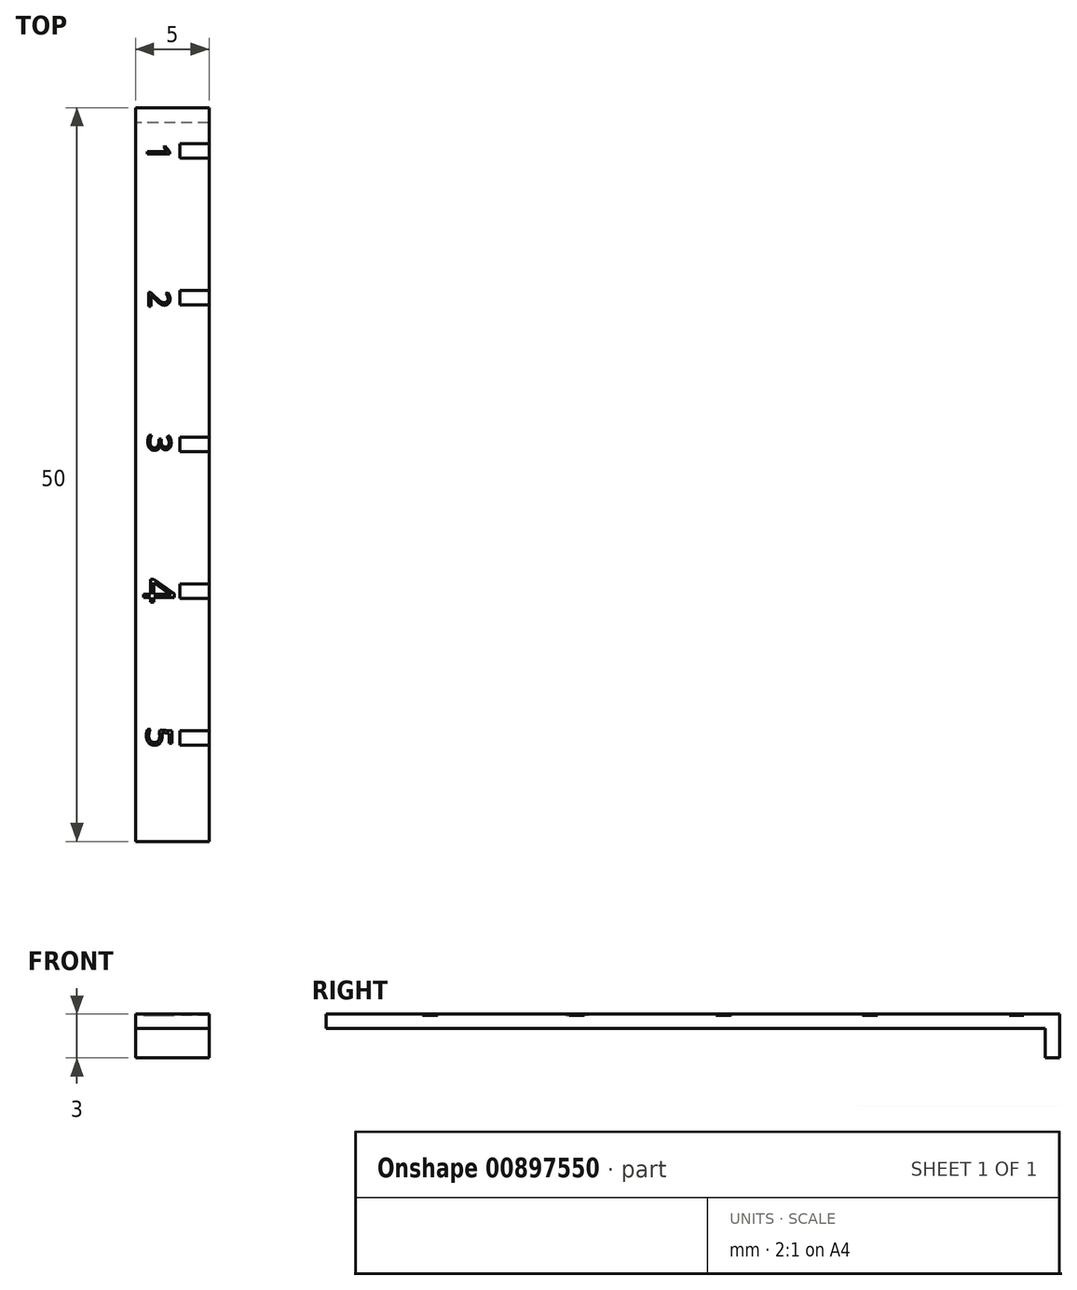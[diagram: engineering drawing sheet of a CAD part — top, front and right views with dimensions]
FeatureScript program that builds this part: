
annotation { "Feature Type Name" : "Feature", "Feature Type Description" : "" }
export const myFeature = defineFeature(function(context is Context, id is Id, definition is map)
    precondition{}
    {
        {
            var Q0;
            Q0=qCreatedBy(makeId("Top.planeOp"),FACE);
            var sketch = newSketch(context, id + "F0", { "sketchPlane" : qUnion([Q0])});
            skLineSegment(sketch, "E0.bottom", {"start": v(-33.65, 38.49) * mm, "end": v(-28.65, 38.49) * mm});
            skLineSegment(sketch, "E0.top", {"start": v(-33.65, -11.51) * mm, "end": v(-28.65, -11.51) * mm});
            skLineSegment(sketch, "E0.left", {"start": v(-33.65, 38.49) * mm, "end": v(-33.65, -11.51) * mm});
            skLineSegment(sketch, "E0.right", {"start": v(-28.65, 38.49) * mm, "end": v(-28.65, -11.51) * mm});
            skSolve(sketch);
        }
        {
            var Q0;
            Q0 = qSketchRegion(id + "F0", true);
            extrude(context, id + "F1", {"entities" : qUnion([Q0]), "depth" : 1 * mm, "offsetDistance" : 25 * mm});
        }
        {
            var Q0;
            Q0=makeQuery(id+"F1.opExtrude","CAP_FACE",FACE,{"disambiguationData":[OSD([sQuery(id+"F0.wireOp",EDGE,"E0.bottom"),sQuery(id+"F0.wireOp",EDGE,"E0.top"),sQuery(id+"F0.wireOp",EDGE,"E0.left"),sQuery(id+"F0.wireOp",EDGE,"E0.right")])],"isStart":true});
            var sketch = newSketch(context, id + "F2", { "sketchPlane" : qUnion([Q0])});
            skLineSegment(sketch, "E1.bottom", {"start": v(-28.65, -38.49) * mm, "end": v(-33.65, -38.49) * mm});
            skLineSegment(sketch, "E1.top", {"start": v(-28.65, -37.49) * mm, "end": v(-33.65, -37.49) * mm});
            skLineSegment(sketch, "E1.left", {"start": v(-28.65, -38.49) * mm, "end": v(-28.65, -37.49) * mm});
            skLineSegment(sketch, "E1.right", {"start": v(-33.65, -38.49) * mm, "end": v(-33.65, -37.49) * mm});
            skSolve(sketch);
        }
        {
            var Q0;
            Q0 = qSketchRegion(id + "F2", true);
            extrude(context, id + "F3", {"entities" : qUnion([Q0]), "operationType" : NewBodyOperationType.ADD, "depth" : 2 * mm, "offsetDistance" : 25 * mm});
        }
        {
            var Q0;
            Q0=makeQuery(id+"F1.opExtrude","CAP_FACE",FACE,{"disambiguationData":[OSD([sQuery(id+"F0.wireOp",EDGE,"E0.bottom"),sQuery(id+"F0.wireOp",EDGE,"E0.top"),sQuery(id+"F0.wireOp",EDGE,"E0.left"),sQuery(id+"F0.wireOp",EDGE,"E0.right")])],"isStart":false});
            var sketch = newSketch(context, id + "F4", { "sketchPlane" : qUnion([Q0])});
            skLineSegment(sketch, "E2.bottom", {"start": v(-28.65, 36.05) * mm, "end": v(-30.65, 36.05) * mm});
            skLineSegment(sketch, "E2.top", {"start": v(-28.65, 35.05) * mm, "end": v(-30.65, 35.05) * mm});
            skLineSegment(sketch, "E2.left", {"start": v(-28.65, 36.05) * mm, "end": v(-28.65, 35.05) * mm});
            skLineSegment(sketch, "E2.right", {"start": v(-30.65, 36.05) * mm, "end": v(-30.65, 35.05) * mm});
            skLineSegment(sketch, "E3.0.1.0", {"start": v(-28.65, 26.05) * mm, "end": v(-28.65, 25.05) * mm});
            skLineSegment(sketch, "E3.0.1.1", {"start": v(-28.65, 25.05) * mm, "end": v(-30.65, 25.05) * mm});
            skLineSegment(sketch, "E3.0.1.2", {"start": v(-30.65, 26.05) * mm, "end": v(-30.65, 25.05) * mm});
            skLineSegment(sketch, "E3.0.1.3", {"start": v(-28.65, 26.05) * mm, "end": v(-30.65, 26.05) * mm});
            skLineSegment(sketch, "E3.0.2.0", {"start": v(-28.65, 16.05) * mm, "end": v(-28.65, 15.05) * mm});
            skLineSegment(sketch, "E3.0.2.1", {"start": v(-28.65, 15.05) * mm, "end": v(-30.65, 15.05) * mm});
            skLineSegment(sketch, "E3.0.2.2", {"start": v(-30.65, 16.05) * mm, "end": v(-30.65, 15.05) * mm});
            skLineSegment(sketch, "E3.0.2.3", {"start": v(-28.65, 16.05) * mm, "end": v(-30.65, 16.05) * mm});
            skLineSegment(sketch, "E3.0.3.0", {"start": v(-28.65, 6.05) * mm, "end": v(-28.65, 5.05) * mm});
            skLineSegment(sketch, "E3.0.3.1", {"start": v(-28.65, 5.05) * mm, "end": v(-30.65, 5.05) * mm});
            skLineSegment(sketch, "E3.0.3.2", {"start": v(-30.65, 6.05) * mm, "end": v(-30.65, 5.05) * mm});
            skLineSegment(sketch, "E3.0.3.3", {"start": v(-28.65, 6.05) * mm, "end": v(-30.65, 6.05) * mm});
            skLineSegment(sketch, "E3.0.4.0", {"start": v(-28.65, -3.95) * mm, "end": v(-28.65, -4.95) * mm});
            skLineSegment(sketch, "E3.0.4.1", {"start": v(-28.65, -4.95) * mm, "end": v(-30.65, -4.95) * mm});
            skLineSegment(sketch, "E3.0.4.2", {"start": v(-30.65, -3.95) * mm, "end": v(-30.65, -4.95) * mm});
            skLineSegment(sketch, "E3.0.4.3", {"start": v(-28.65, -3.95) * mm, "end": v(-30.65, -3.95) * mm});
            skLineSegment(sketch, "E3.1.1.0", {"start": v(-28.65, 26.05) * mm, "end": v(-28.65, 25.05) * mm});
            skLineSegment(sketch, "E3.1.1.1", {"start": v(-28.65, 25.05) * mm, "end": v(-30.65, 25.05) * mm});
            skLineSegment(sketch, "E3.1.1.2", {"start": v(-30.65, 26.05) * mm, "end": v(-30.65, 25.05) * mm});
            skLineSegment(sketch, "E3.1.1.3", {"start": v(-28.65, 26.05) * mm, "end": v(-30.65, 26.05) * mm});
            skLineSegment(sketch, "E3.1.2.0", {"start": v(-28.65, 16.05) * mm, "end": v(-28.65, 15.05) * mm});
            skLineSegment(sketch, "E3.1.2.1", {"start": v(-28.65, 15.05) * mm, "end": v(-30.65, 15.05) * mm});
            skLineSegment(sketch, "E3.1.2.2", {"start": v(-30.65, 16.05) * mm, "end": v(-30.65, 15.05) * mm});
            skLineSegment(sketch, "E3.1.2.3", {"start": v(-28.65, 16.05) * mm, "end": v(-30.65, 16.05) * mm});
            skLineSegment(sketch, "E3.1.3.0", {"start": v(-28.65, 6.05) * mm, "end": v(-28.65, 5.05) * mm});
            skLineSegment(sketch, "E3.1.3.1", {"start": v(-28.65, 5.05) * mm, "end": v(-30.65, 5.05) * mm});
            skLineSegment(sketch, "E3.1.3.2", {"start": v(-30.65, 6.05) * mm, "end": v(-30.65, 5.05) * mm});
            skLineSegment(sketch, "E3.1.3.3", {"start": v(-28.65, 6.05) * mm, "end": v(-30.65, 6.05) * mm});
            skLineSegment(sketch, "E3.1.4.0", {"start": v(-28.65, -3.95) * mm, "end": v(-28.65, -4.95) * mm});
            skLineSegment(sketch, "E3.1.4.1", {"start": v(-28.65, -4.95) * mm, "end": v(-30.65, -4.95) * mm});
            skLineSegment(sketch, "E3.1.4.2", {"start": v(-30.65, -3.95) * mm, "end": v(-30.65, -4.95) * mm});
            skLineSegment(sketch, "E3.1.4.3", {"start": v(-28.65, -3.95) * mm, "end": v(-30.65, -3.95) * mm});
            skLineSegment(sketch, "E3.2.1.0", {"start": v(-28.65, 26.05) * mm, "end": v(-28.65, 25.05) * mm});
            skLineSegment(sketch, "E3.2.1.1", {"start": v(-28.65, 25.05) * mm, "end": v(-30.65, 25.05) * mm});
            skLineSegment(sketch, "E3.2.1.2", {"start": v(-30.65, 26.05) * mm, "end": v(-30.65, 25.05) * mm});
            skLineSegment(sketch, "E3.2.1.3", {"start": v(-28.65, 26.05) * mm, "end": v(-30.65, 26.05) * mm});
            skLineSegment(sketch, "E3.2.2.0", {"start": v(-28.65, 16.05) * mm, "end": v(-28.65, 15.05) * mm});
            skLineSegment(sketch, "E3.2.2.1", {"start": v(-28.65, 15.05) * mm, "end": v(-30.65, 15.05) * mm});
            skLineSegment(sketch, "E3.2.2.2", {"start": v(-30.65, 16.05) * mm, "end": v(-30.65, 15.05) * mm});
            skLineSegment(sketch, "E3.2.2.3", {"start": v(-28.65, 16.05) * mm, "end": v(-30.65, 16.05) * mm});
            skLineSegment(sketch, "E3.2.3.0", {"start": v(-28.65, 6.05) * mm, "end": v(-28.65, 5.05) * mm});
            skLineSegment(sketch, "E3.2.3.1", {"start": v(-28.65, 5.05) * mm, "end": v(-30.65, 5.05) * mm});
            skLineSegment(sketch, "E3.2.3.2", {"start": v(-30.65, 6.05) * mm, "end": v(-30.65, 5.05) * mm});
            skLineSegment(sketch, "E3.2.3.3", {"start": v(-28.65, 6.05) * mm, "end": v(-30.65, 6.05) * mm});
            skLineSegment(sketch, "E3.2.4.0", {"start": v(-28.65, -3.95) * mm, "end": v(-28.65, -4.95) * mm});
            skLineSegment(sketch, "E3.2.4.1", {"start": v(-28.65, -4.95) * mm, "end": v(-30.65, -4.95) * mm});
            skLineSegment(sketch, "E3.2.4.2", {"start": v(-30.65, -3.95) * mm, "end": v(-30.65, -4.95) * mm});
            skLineSegment(sketch, "E3.2.4.3", {"start": v(-28.65, -3.95) * mm, "end": v(-30.65, -3.95) * mm});
            skLineSegment(sketch, "E3.direction1", {"start": v(-30.65, 35.05) * mm, "end": v(-30.65, 35.05) * mm});
            skLineSegment(sketch, "E3.direction2", {"start": v(-30.65, 35.05) * mm, "end": v(-30.65, 25.05) * mm, "construction": true});
            skSolve(sketch);
        }
        {
            var Q0;
            Q0 = qSketchRegion(id + "F4", true);
            var Q1;
            Q1 = qConstructionFilter(qBodyType(qCreatedBy(id + "F4" ,EDGE), BodyType.WIRE), ConstructionObject.NO);
            extrude(context, id + "F5", {"entities" : qUnion([Q0]), "operationType" : NewBodyOperationType.REMOVE, "surfaceEntities" : qUnion([Q1]), "oppositeDirection" : true, "depth" : 0.1 * mm, "offsetDistance" : 25 * mm});
        }
        {
            var Q0;
            Q0=makeQuery(id+"F1.opExtrude","CAP_FACE",FACE,{"disambiguationData":[OSD([sQuery(id+"F0.wireOp",EDGE,"E0.bottom"),sQuery(id+"F0.wireOp",EDGE,"E0.top"),sQuery(id+"F0.wireOp",EDGE,"E0.left"),sQuery(id+"F0.wireOp",EDGE,"E0.right")])],"isStart":false});
            var sketch = newSketch(context, id + "F6", { "sketchPlane" : qUnion([Q0])});
            skText(sketch, "E4", { "text": "1", "fontName": "OpenSans-Regular.ttf"});
            skText(sketch, "E5", { "text": "2", "fontName": "OpenSans-Regular.ttf"});
            skText(sketch, "E6", { "text": "3", "fontName": "OpenSans-Regular.ttf"});
            skText(sketch, "E7", { "text": "4", "fontName": "OpenSans-Regular.ttf"});
            skText(sketch, "E8", { "text": "5", "fontName": "OpenSans-Regular.ttf"});
            const initialGuessF6  = {"E4": [-0.03286, 0.0361, 0, -1, 0.00155], "E5": [-0.03277, 0.02603, 0, -1, 0.00146], "E6": [-0.0328, 0.01626, 0, -1, 0.00157], "E7": [-0.0331, 0.00642, 0, -1, 0.0021], "E8": [-0.0329, -0.00371, 0, -1, 0.00174]};
            skSetInitialGuess(sketch, initialGuessF6);
            skSolve(sketch);
        }
        {
            var Q0;
            Q0 = qSketchRegion(id + "F6", true);
            extrude(context, id + "F7", {"entities" : qUnion([Q0]), "operationType" : NewBodyOperationType.REMOVE, "oppositeDirection" : true, "depth" : 0.1 * mm, "offsetDistance" : 25 * mm});
        }
    });
